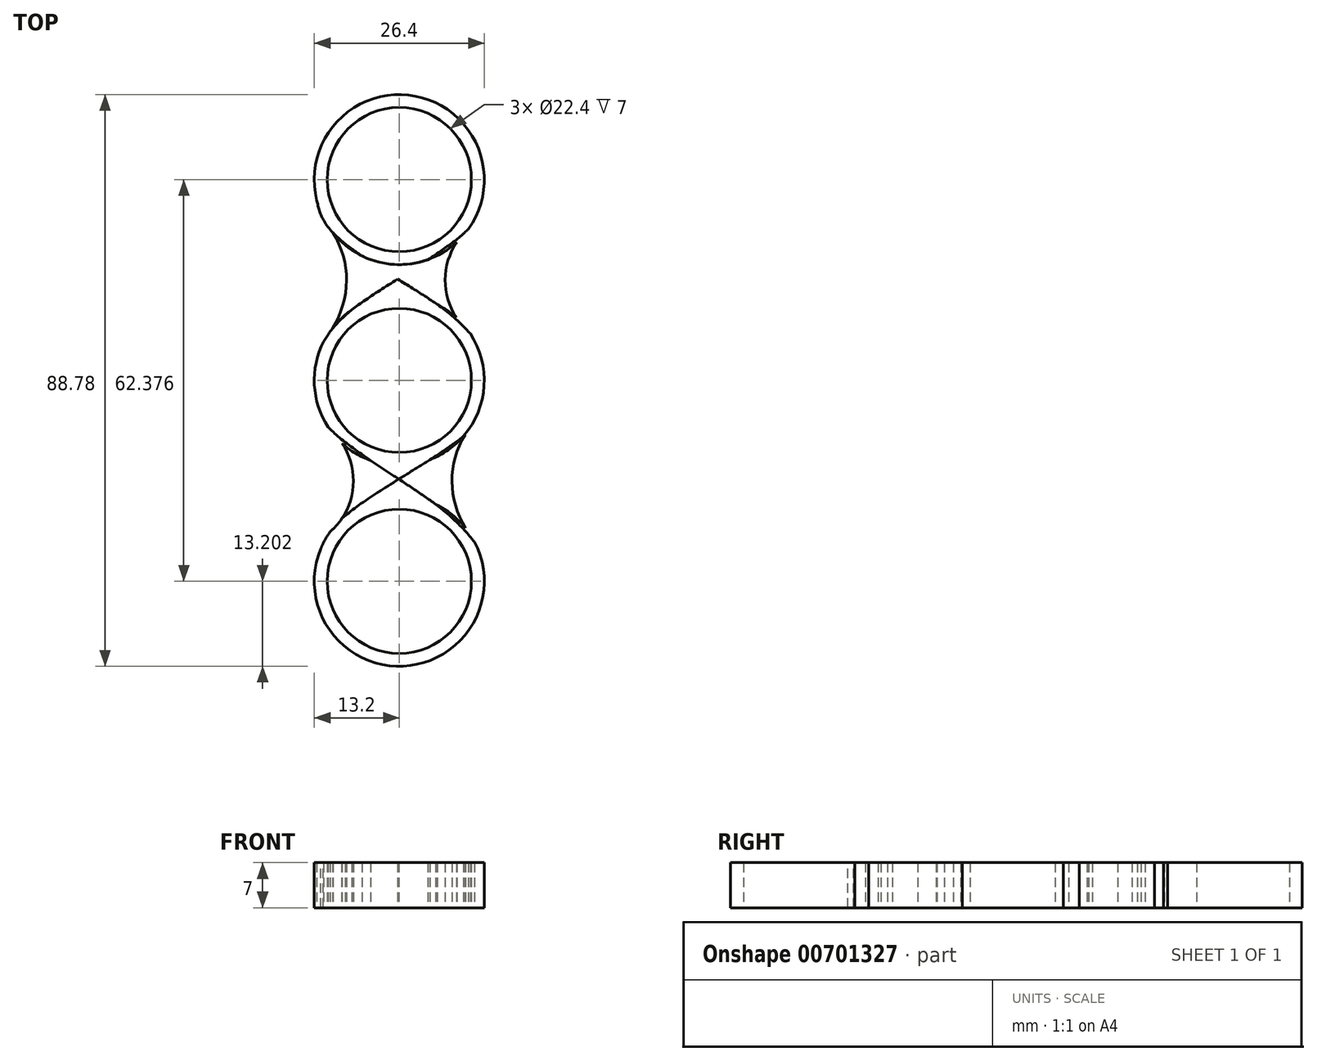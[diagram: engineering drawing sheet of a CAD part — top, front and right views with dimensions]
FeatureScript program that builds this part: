
annotation { "Feature Type Name" : "Feature", "Feature Type Description" : "" }
export const myFeature = defineFeature(function(context is Context, id is Id, definition is map)
    precondition{}
    {
        {
            var Q0;
            Q0=qCreatedBy(makeId("Top.planeOp"),FACE);
            var sketch = newSketch(context, id + "F0", { "sketchPlane" : qUnion([Q0])});
            skCircle(sketch, "E0", {"center": v(0, 0) * mm, "radius": 11.2 * mm});
            skCircle(sketch, "E1", {"center": v(0, 0) * mm, "radius": 13.2 * mm});
            skCircle(sketch, "E2", {"center": v(0, 31.19) * mm, "radius": 13.2 * mm});
            skCircle(sketch, "E3", {"center": v(0, 31.19) * mm, "radius": 11.2 * mm});
            skCircle(sketch, "E4.1.0", {"center": v(0, -31.19) * mm, "radius": 13.2 * mm});
            skCircle(sketch, "E4.1.1", {"center": v(0, -31.19) * mm, "radius": 11.2 * mm});
            skFitSpline(sketch, "E5", {"points": [v(-12.8, 27.96) * mm, v(-10.3, 22.94) * mm, v(5.88, 11.82) * mm, v(11.02, 7.27) * mm], "startDerivative": vector(4.16, -18.87) * mm, "endDerivative": vector(13.55, -14.62) * mm});
            skFitSpline(sketch, "E6", {"points": [v(12.62, 27.33) * mm, v(10.71, 23.48) * mm, v(-7.34, 10.97) * mm, v(-11.74, 6.04) * mm], "startDerivative": vector(-2.94, -15.59) * mm, "endDerivative": vector(-10, -16.07) * mm});
            skFitSpline(sketch, "E7", {"points": [v(-12.8, -3.25) * mm, v(-11.06, -7.21) * mm, v(5.67, -19.27) * mm, v(11.7, -25.09) * mm], "startDerivative": vector(2.3, -16.6) * mm, "endDerivative": vector(14.45, -17.33) * mm});
            skFitSpline(sketch, "E8", {"points": [v(11.9, -5.7) * mm, v(10, -8.62) * mm, v(-8.39, -21) * mm, v(-12.22, -26.2) * mm], "startDerivative": vector(-3.94, -12.4) * mm, "endDerivative": vector(-7.47, -16.94) * mm});
            skArc(sketch, "E9", {"start": v(10.71, 23.48) * mm, "mid": v(7.15, 16.25) * mm, "end": v(9.76, 8.63) * mm});
            skArc(sketch, "E10", {"start": v(-10.82, 7.52) * mm, "mid": v(-8.2, 15.15) * mm, "end": v(-10.3, 22.94) * mm});
            skArc(sketch, "E11", {"start": v(11.63, -6.56) * mm, "mid": v(11.15, -7.22) * mm, "end": v(10.7, -7.91) * mm});
            skArc(sketch, "E12.trimOffspring", {"start": v(9.73, -22.27) * mm, "mid": v(9.98, -22.8) * mm, "end": v(10.24, -23.33) * mm});
            skArc(sketch, "E13.1.0", {"start": v(-10.71, -23.48) * mm, "mid": v(-7.15, -16.25) * mm, "end": v(-9.76, -8.63) * mm});
            skArc(sketch, "E13.1.1", {"start": v(10.82, -7.52) * mm, "mid": v(8.2, -15.15) * mm, "end": v(10.3, -22.94) * mm});
            skSolve(sketch);
        }
        {
            var Q0;
            Q0=makeQuery(id+"F0.imprint","IMPRINT",FACE,{"disambiguationData":[TD([[makeQuery(id+"F0.imprint","IMPRINT",EDGE,{"derivedFrom":sQuery(id+"F0.wireOp",EDGE,"E3")}),-1.0]])]});
            var Q1;
            {var subQ0=sQuery(id+"F0.wireOp",EDGE,"E5");var subQ1=sQuery(id+"F0.wireOp",EDGE,"E2");var subQ2=makeQuery(id+"F0.imprint","INTERSECT",VERTEX,{"disambiguationData":[OD(2.0)],"derivedFrom":[subQ1,subQ0]});Q1=makeQuery(id+"F0.imprint","IMPRINT",FACE,{"disambiguationData":[TD([[makeQuery(id+"F0.imprint","IMPRINT",EDGE,{"disambiguationData":[TD([[subQ2,-1.0]])],"derivedFrom":subQ1}),-1.0]])]});}
            var Q2;
            {var subQ0=sQuery(id+"F0.wireOp",EDGE,"E5");var subQ1=sQuery(id+"F0.wireOp",EDGE,"E1");var subQ2=makeQuery(id+"F0.imprint","INTERSECT",VERTEX,{"disambiguationData":[OD(1.0)],"derivedFrom":[subQ1,subQ0]});Q2=makeQuery(id+"F0.imprint","IMPRINT",FACE,{"disambiguationData":[TD([[makeQuery(id+"F0.imprint","IMPRINT",EDGE,{"disambiguationData":[TD([[subQ2,-1.0]])],"derivedFrom":subQ1}),-1.0]])]});}
            var Q3;
            Q3=makeQuery(id+"F0.imprint","IMPRINT",FACE,{"disambiguationData":[TD([[makeQuery(id+"F0.imprint","IMPRINT",EDGE,{"derivedFrom":sQuery(id+"F0.wireOp",EDGE,"E0")}),-1.0]])]});
            var Q4;
            {var subQ0=sQuery(id+"F0.wireOp",EDGE,"E7");var subQ1=sQuery(id+"F0.wireOp",EDGE,"E4.1.0");var subQ2=makeQuery(id+"F0.imprint","INTERSECT",VERTEX,{"disambiguationData":[OD(1.0)],"derivedFrom":[subQ1,subQ0]});Q4=makeQuery(id+"F0.imprint","IMPRINT",FACE,{"disambiguationData":[TD([[makeQuery(id+"F0.imprint","IMPRINT",EDGE,{"disambiguationData":[TD([[subQ2,-1.0]])],"derivedFrom":subQ1}),-1.0]])]});}
            var Q5;
            {var subQ0=sQuery(id+"F0.wireOp",EDGE,"E7");var subQ1=sQuery(id+"F0.wireOp",EDGE,"E1");var subQ2=makeQuery(id+"F0.imprint","INTERSECT",VERTEX,{"disambiguationData":[OD(2.0)],"derivedFrom":[subQ1,subQ0]});Q5=makeQuery(id+"F0.imprint","IMPRINT",FACE,{"disambiguationData":[TD([[makeQuery(id+"F0.imprint","IMPRINT",EDGE,{"disambiguationData":[TD([[subQ2,-1.0]])],"derivedFrom":subQ1}),-1.0]])]});}
            var Q6;
            Q6=makeQuery(id+"F0.imprint","IMPRINT",FACE,{"disambiguationData":[TD([[makeQuery(id+"F0.imprint","IMPRINT",EDGE,{"derivedFrom":sQuery(id+"F0.wireOp",EDGE,"E4.1.1")}),-1.0]])]});
            extrude(context, id + "F1", {"entities" : qUnion([Q0, Q1, Q2, Q3, Q4, Q5, Q6]), "depth" : 7 * mm, "offsetDistance" : 25 * mm});
        }
        {
            var Q0;
            {var subQ0=sQuery(id+"F0.wireOp",EDGE,"E9");var subQ7=sQuery(id+"F0.wireOp",EDGE,"E1");var subQ9=makeQuery(id+"F0.imprint","INTERSECT",VERTEX,{"derivedFrom":[subQ7,subQ0]});Q0=makeQuery(id+"F0.imprint","IMPRINT",FACE,{"disambiguationData":[TD([[makeQuery(id+"F0.imprint","IMPRINT",EDGE,{"disambiguationData":[TD([[subQ9,-1.0]])],"derivedFrom":subQ7}),-1.0]])]});}
            var Q1;
            {var subQ0=sQuery(id+"F0.wireOp",EDGE,"E5");var subQ1=sQuery(id+"F0.wireOp",EDGE,"E2");var subQ2=makeQuery(id+"F0.imprint","INTERSECT",VERTEX,{"disambiguationData":[OD(1.0)],"derivedFrom":[subQ1,subQ0]});Q1=makeQuery(id+"F0.imprint","IMPRINT",FACE,{"disambiguationData":[TD([[makeQuery(id+"F0.imprint","IMPRINT",EDGE,{"disambiguationData":[TD([[subQ2,-1.0]])],"derivedFrom":subQ1}),-1.0]])]});}
            var Q2;
            {var subQ1=sQuery(id+"F0.wireOp",EDGE,"E1");var subQ7=sQuery(id+"F0.wireOp",EDGE,"E10");var subQ9=makeQuery(id+"F0.imprint","INTERSECT",VERTEX,{"derivedFrom":[subQ1,subQ7]});Q2=makeQuery(id+"F0.imprint","IMPRINT",FACE,{"disambiguationData":[TD([[makeQuery(id+"F0.imprint","IMPRINT",EDGE,{"disambiguationData":[TD([[subQ9,1.0]])],"derivedFrom":subQ1}),-1.0]])]});}
            var Q3;
            {var subQ1=sQuery(id+"F0.wireOp",EDGE,"E4.1.0");var subQ8=makeQuery(id+"F0.imprint","IMPRINT",VERTEX,{"derivedFrom":subQ1});Q3=makeQuery(id+"F0.imprint","IMPRINT",FACE,{"disambiguationData":[TD([[makeQuery(id+"F0.imprint","IMPRINT",EDGE,{"disambiguationData":[TD([[subQ8,1.0]])],"derivedFrom":subQ1}),-1.0]])]});}
            var Q4;
            {var subQ5=sQuery(id+"F0.wireOp",EDGE,"E1");var subQ7=sQuery(id+"F0.wireOp",EDGE,"E13.1.0");var subQ9=makeQuery(id+"F0.imprint","INTERSECT",VERTEX,{"derivedFrom":[subQ5,subQ7]});Q4=makeQuery(id+"F0.imprint","IMPRINT",FACE,{"disambiguationData":[TD([[makeQuery(id+"F0.imprint","IMPRINT",EDGE,{"disambiguationData":[TD([[subQ9,-1.0]])],"derivedFrom":subQ5}),-1.0]])]});}
            extrude(context, id + "F2", {"entities" : qUnion([Q0, Q1, Q2, Q3, Q4]), "depth" : 7 * mm, "offsetDistance" : 25 * mm});
        }
    });
